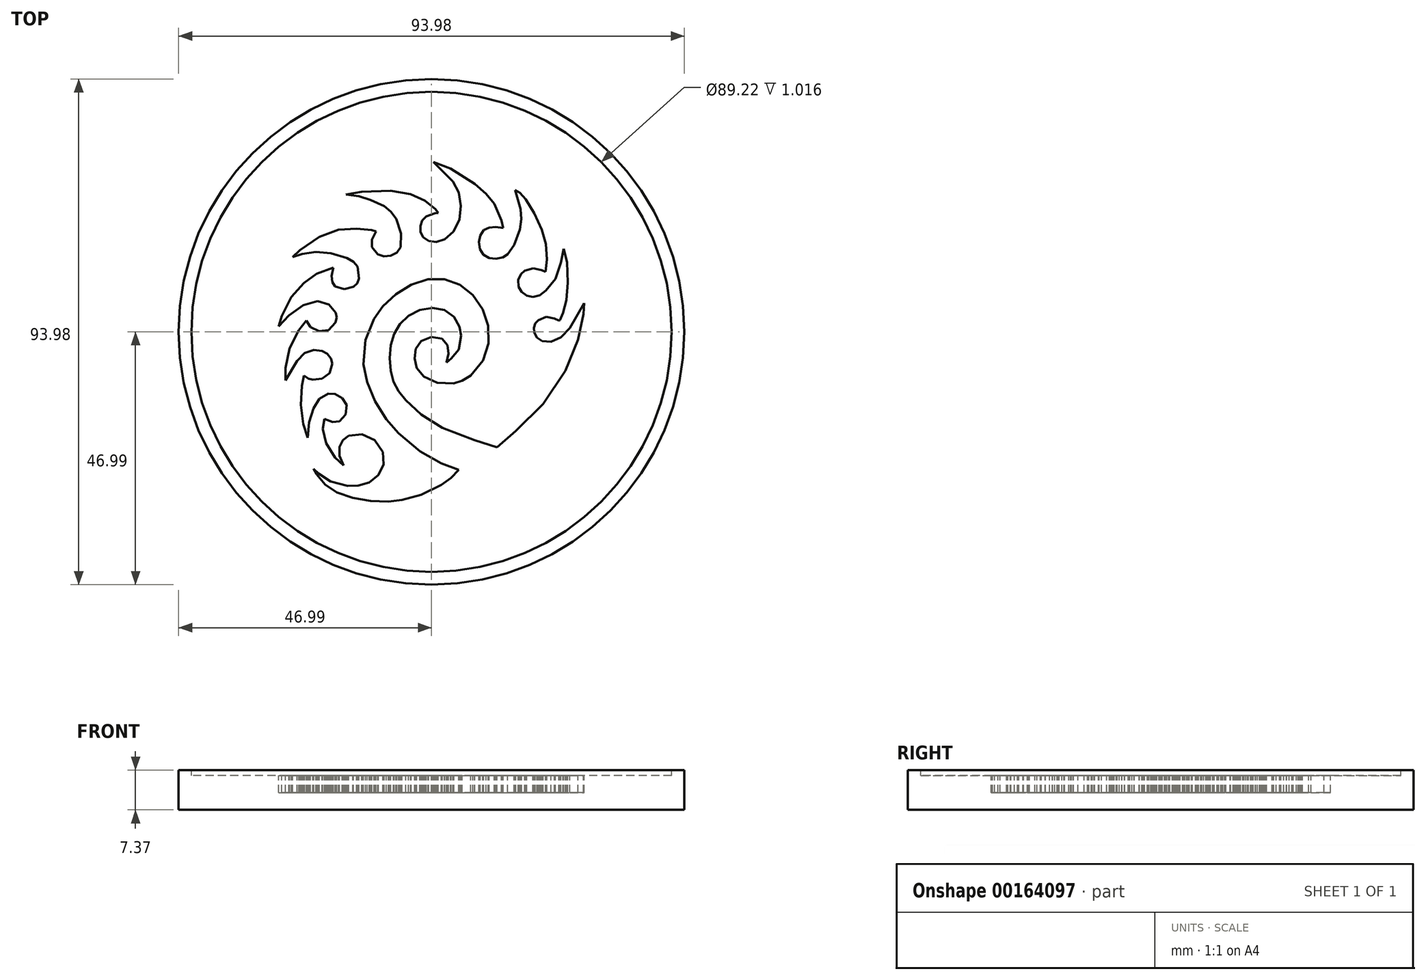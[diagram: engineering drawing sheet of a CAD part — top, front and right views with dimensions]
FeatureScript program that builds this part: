
annotation { "Feature Type Name" : "Feature", "Feature Type Description" : "" }
export const myFeature = defineFeature(function(context is Context, id is Id, definition is map)
    precondition{}
    {
        {
            var Q0;
            Q0=qCreatedBy(makeId("Front.planeOp"),FACE);
            var sketch = newSketch(context, id + "F0", { "sketchPlane" : qUnion([Q0])});
            skLineSegment(sketch, "E0", {"start": v(-47, 7.37) * mm, "end": v(-44.6, 7.37) * mm});
            skLineSegment(sketch, "E1", {"start": v(-44.6, 7.37) * mm, "end": v(-44.6, 6.35) * mm});
            skLineSegment(sketch, "E2", {"start": v(-44.6, 6.35) * mm, "end": v(0, 6.35) * mm});
            skLineSegment(sketch, "E3", {"start": v(0, 6.35) * mm, "end": v(0, 0) * mm});
            skLineSegment(sketch, "E4", {"start": v(0, 0) * mm, "end": v(-47, 0) * mm});
            skLineSegment(sketch, "E5", {"start": v(-47, 0) * mm, "end": v(-47, 7.37) * mm});
            skSolve(sketch);
        }
        {
            var Q0;
            Q0=makeQuery(id+"F0.imprint","IMPRINT",FACE,{"disambiguationData":[TD([[makeQuery(id+"F0.imprint","IMPRINT",EDGE,{"derivedFrom":sQuery(id+"F0.wireOp",EDGE,"E0")}),-1.0]])]});
            var Q1;
            Q1=sQuery(id+"F0.wireOp",EDGE,"E3");
            revolve(context, id + "F1", {"entities" : qUnion([Q0]), "axis" : qUnion([Q1]), "revolveType" : RevolveType.FULL});
        }
        {
            var Q0;
            Q0=makeQuery(id+"F1.opRevolve","SWEPT_FACE",FACE,{"disambiguationData":[OSD([sQuery(id+"F0.wireOp",EDGE,"E2")])]});
            var sketch = newSketch(context, id + "F2", { "sketchPlane" : qUnion([Q0])});
            skLineSegment(sketch, "E6", {"start": v(3.51, 30.35) * mm, "end": v(8.02, 27.48) * mm});
            skLineSegment(sketch, "E7", {"start": v(8.02, 27.48) * mm, "end": v(10.13, 25.64) * mm});
            skLineSegment(sketch, "E8", {"start": v(10.13, 25.64) * mm, "end": v(11.64, 23.83) * mm});
            skLineSegment(sketch, "E9", {"start": v(11.64, 23.83) * mm, "end": v(13.01, 20.73) * mm});
            skLineSegment(sketch, "E10", {"start": v(13.01, 20.73) * mm, "end": v(13.3, 19.34) * mm});
            skLineSegment(sketch, "E11", {"start": v(13.3, 19.34) * mm, "end": v(11.92, 19.48) * mm});
            skLineSegment(sketch, "E12", {"start": v(11.92, 19.48) * mm, "end": v(10.73, 19.38) * mm});
            skLineSegment(sketch, "E13", {"start": v(10.73, 19.38) * mm, "end": v(9.7, 18.9) * mm});
            skLineSegment(sketch, "E14", {"start": v(9.7, 18.9) * mm, "end": v(9.07, 17.93) * mm});
            skLineSegment(sketch, "E15", {"start": v(9.07, 17.93) * mm, "end": v(8.83, 16.67) * mm});
            skLineSegment(sketch, "E16", {"start": v(8.83, 16.67) * mm, "end": v(9.01, 15.38) * mm});
            skLineSegment(sketch, "E17", {"start": v(9.01, 15.38) * mm, "end": v(9.65, 14.33) * mm});
            skLineSegment(sketch, "E18", {"start": v(9.65, 14.33) * mm, "end": v(10.72, 13.72) * mm});
            skLineSegment(sketch, "E19", {"start": v(10.72, 13.72) * mm, "end": v(12, 13.57) * mm});
            skLineSegment(sketch, "E20", {"start": v(12, 13.57) * mm, "end": v(13.24, 13.81) * mm});
            skLineSegment(sketch, "E21", {"start": v(13.24, 13.81) * mm, "end": v(14.14, 14.4) * mm});
            skLineSegment(sketch, "E22", {"start": v(14.14, 14.4) * mm, "end": v(15.38, 16.13) * mm});
            skLineSegment(sketch, "E23", {"start": v(15.38, 16.13) * mm, "end": v(16.44, 19.06) * mm});
            skLineSegment(sketch, "E24", {"start": v(16.44, 19.06) * mm, "end": v(16.7, 20.97) * mm});
            skLineSegment(sketch, "E25", {"start": v(16.7, 20.97) * mm, "end": v(16.58, 22.8) * mm});
            skLineSegment(sketch, "E26", {"start": v(16.58, 22.8) * mm, "end": v(15.56, 26.32) * mm});
            skLineSegment(sketch, "E27", {"start": v(15.56, 26.32) * mm, "end": v(16.4, 25.85) * mm});
            skLineSegment(sketch, "E28", {"start": v(16.4, 25.85) * mm, "end": v(17.54, 24.62) * mm});
            skLineSegment(sketch, "E29", {"start": v(17.54, 24.62) * mm, "end": v(19.11, 22.05) * mm});
            skLineSegment(sketch, "E30", {"start": v(19.11, 22.05) * mm, "end": v(20.52, 18.99) * mm});
            skLineSegment(sketch, "E31", {"start": v(20.52, 18.99) * mm, "end": v(21.26, 16.32) * mm});
            skLineSegment(sketch, "E32", {"start": v(21.26, 16.32) * mm, "end": v(21.47, 13.44) * mm});
            skLineSegment(sketch, "E33", {"start": v(21.47, 13.44) * mm, "end": v(21.2, 11.14) * mm});
            skLineSegment(sketch, "E34", {"start": v(21.2, 11.14) * mm, "end": v(20.38, 11.51) * mm});
            skLineSegment(sketch, "E35", {"start": v(20.38, 11.51) * mm, "end": v(18.88, 11.82) * mm});
            skLineSegment(sketch, "E36", {"start": v(18.88, 11.82) * mm, "end": v(17.3, 11.38) * mm});
            skLineSegment(sketch, "E37", {"start": v(17.3, 11.38) * mm, "end": v(16.6, 10.73) * mm});
            skLineSegment(sketch, "E38", {"start": v(16.6, 10.73) * mm, "end": v(16.13, 9.64) * mm});
            skLineSegment(sketch, "E39", {"start": v(16.13, 9.64) * mm, "end": v(16.15, 8.39) * mm});
            skLineSegment(sketch, "E40", {"start": v(16.15, 8.39) * mm, "end": v(16.72, 7.4) * mm});
            skLineSegment(sketch, "E41", {"start": v(16.72, 7.4) * mm, "end": v(17.67, 6.75) * mm});
            skLineSegment(sketch, "E42", {"start": v(17.67, 6.75) * mm, "end": v(18.87, 6.5) * mm});
            skLineSegment(sketch, "E43", {"start": v(18.87, 6.5) * mm, "end": v(20.1, 6.82) * mm});
            skLineSegment(sketch, "E44", {"start": v(20.1, 6.82) * mm, "end": v(21.26, 7.67) * mm});
            skLineSegment(sketch, "E45", {"start": v(21.26, 7.67) * mm, "end": v(23.02, 9.87) * mm});
            skLineSegment(sketch, "E46", {"start": v(23.02, 9.87) * mm, "end": v(24.07, 12.88) * mm});
            skLineSegment(sketch, "E47", {"start": v(24.07, 12.88) * mm, "end": v(24.53, 15.44) * mm});
            skLineSegment(sketch, "E48", {"start": v(24.53, 15.44) * mm, "end": v(25.18, 12.95) * mm});
            skLineSegment(sketch, "E49", {"start": v(25.18, 12.95) * mm, "end": v(25.34, 9.11) * mm});
            skLineSegment(sketch, "E50", {"start": v(25.34, 9.11) * mm, "end": v(25.05, 5.9) * mm});
            skLineSegment(sketch, "E51", {"start": v(25.05, 5.9) * mm, "end": v(24.41, 3.51) * mm});
            skLineSegment(sketch, "E52", {"start": v(24.41, 3.51) * mm, "end": v(23.83, 2.2) * mm});
            skLineSegment(sketch, "E53", {"start": v(23.83, 2.2) * mm, "end": v(23.67, 2.11) * mm});
            skLineSegment(sketch, "E54", {"start": v(23.67, 2.11) * mm, "end": v(22.83, 2.47) * mm});
            skLineSegment(sketch, "E55", {"start": v(22.83, 2.47) * mm, "end": v(21.3, 2.77) * mm});
            skLineSegment(sketch, "E56", {"start": v(21.3, 2.77) * mm, "end": v(19.84, 2.17) * mm});
            skLineSegment(sketch, "E57", {"start": v(19.84, 2.17) * mm, "end": v(19.27, 1.56) * mm});
            skLineSegment(sketch, "E58", {"start": v(19.27, 1.56) * mm, "end": v(19.02, 0.78) * mm});
            skLineSegment(sketch, "E59", {"start": v(19.02, 0.78) * mm, "end": v(19.11, -0.16) * mm});
            skLineSegment(sketch, "E60", {"start": v(19.11, -0.16) * mm, "end": v(19.59, -1.07) * mm});
            skLineSegment(sketch, "E61", {"start": v(19.59, -1.07) * mm, "end": v(20.57, -1.73) * mm});
            skLineSegment(sketch, "E62", {"start": v(20.57, -1.73) * mm, "end": v(22.18, -1.86) * mm});
            skLineSegment(sketch, "E63", {"start": v(22.18, -1.86) * mm, "end": v(24.06, -1.05) * mm});
            skLineSegment(sketch, "E64", {"start": v(24.06, -1.05) * mm, "end": v(25.71, 0.7) * mm});
            skLineSegment(sketch, "E65", {"start": v(25.71, 0.7) * mm, "end": v(28.38, 5.32) * mm});
            skLineSegment(sketch, "E66", {"start": v(28.38, 5.32) * mm, "end": v(28.23, 3.3) * mm});
            skLineSegment(sketch, "E67", {"start": v(28.23, 3.3) * mm, "end": v(27.24, -1.5) * mm});
            skLineSegment(sketch, "E68", {"start": v(27.24, -1.5) * mm, "end": v(24.85, -7.22) * mm});
            skLineSegment(sketch, "E69", {"start": v(24.85, -7.22) * mm, "end": v(20.72, -13.37) * mm});
            skLineSegment(sketch, "E70", {"start": v(20.72, -13.37) * mm, "end": v(15.7, -18.4) * mm});
            skLineSegment(sketch, "E71", {"start": v(15.7, -18.4) * mm, "end": v(12.17, -21.48) * mm});
            skLineSegment(sketch, "E72", {"start": v(12.17, -21.48) * mm, "end": v(8, -20.13) * mm});
            skLineSegment(sketch, "E73", {"start": v(8, -20.13) * mm, "end": v(2.04, -17.87) * mm});
            skLineSegment(sketch, "E74", {"start": v(2.04, -17.87) * mm, "end": v(-1.91, -15.38) * mm});
            skLineSegment(sketch, "E75", {"start": v(-1.91, -15.38) * mm, "end": v(-4.77, -12.71) * mm});
            skLineSegment(sketch, "E76", {"start": v(-4.77, -12.71) * mm, "end": v(-6.12, -11.02) * mm});
            skLineSegment(sketch, "E77", {"start": v(-6.12, -11.02) * mm, "end": v(-7.05, -9.25) * mm});
            skLineSegment(sketch, "E78", {"start": v(-7.05, -9.25) * mm, "end": v(-7.6, -7.25) * mm});
            skLineSegment(sketch, "E79", {"start": v(-7.6, -7.25) * mm, "end": v(-7.8, -4.9) * mm});
            skLineSegment(sketch, "E80", {"start": v(-7.8, -4.9) * mm, "end": v(-7.6, -2.48) * mm});
            skLineSegment(sketch, "E81", {"start": v(-7.6, -2.48) * mm, "end": v(-6.96, -0.37) * mm});
            skLineSegment(sketch, "E82", {"start": v(-6.96, -0.37) * mm, "end": v(-5.85, 1.44) * mm});
            skLineSegment(sketch, "E83", {"start": v(-5.85, 1.44) * mm, "end": v(-4.26, 2.97) * mm});
            skLineSegment(sketch, "E84", {"start": v(-4.26, 2.97) * mm, "end": v(-2.17, 4.06) * mm});
            skLineSegment(sketch, "E85", {"start": v(-2.17, 4.06) * mm, "end": v(0.18, 4.47) * mm});
            skLineSegment(sketch, "E86", {"start": v(0.18, 4.47) * mm, "end": v(2.43, 4.07) * mm});
            skLineSegment(sketch, "E87", {"start": v(2.43, 4.07) * mm, "end": v(4.18, 2.76) * mm});
            skLineSegment(sketch, "E88", {"start": v(4.18, 2.76) * mm, "end": v(5.18, 0.98) * mm});
            skLineSegment(sketch, "E89", {"start": v(5.18, 0.98) * mm, "end": v(5.52, -0.7) * mm});
            skLineSegment(sketch, "E90", {"start": v(5.52, -0.7) * mm, "end": v(5.04, -3.27) * mm});
            skLineSegment(sketch, "E91", {"start": v(5.04, -3.27) * mm, "end": v(3.7, -4.95) * mm});
            skLineSegment(sketch, "E92", {"start": v(3.7, -4.95) * mm, "end": v(2.76, -5.74) * mm});
            skLineSegment(sketch, "E93", {"start": v(2.76, -5.74) * mm, "end": v(3.18, -4.05) * mm});
            skLineSegment(sketch, "E94", {"start": v(3.18, -4.05) * mm, "end": v(2.95, -2.45) * mm});
            skLineSegment(sketch, "E95", {"start": v(2.95, -2.45) * mm, "end": v(1.94, -1.3) * mm});
            skLineSegment(sketch, "E96", {"start": v(1.94, -1.3) * mm, "end": v(0, -0.98) * mm});
            skLineSegment(sketch, "E97", {"start": v(0, -0.98) * mm, "end": v(-1.94, -1.7) * mm});
            skLineSegment(sketch, "E98", {"start": v(-1.94, -1.7) * mm, "end": v(-2.93, -3.17) * mm});
            skLineSegment(sketch, "E99", {"start": v(-2.93, -3.17) * mm, "end": v(-3.15, -4.98) * mm});
            skLineSegment(sketch, "E100", {"start": v(-3.15, -4.98) * mm, "end": v(-2.78, -6.74) * mm});
            skLineSegment(sketch, "E101", {"start": v(-2.78, -6.74) * mm, "end": v(-1.43, -8.31) * mm});
            skLineSegment(sketch, "E102", {"start": v(-1.43, -8.31) * mm, "end": v(1.04, -9.45) * mm});
            skLineSegment(sketch, "E103", {"start": v(1.04, -9.45) * mm, "end": v(4.11, -9.57) * mm});
            skLineSegment(sketch, "E104", {"start": v(4.11, -9.57) * mm, "end": v(5.7, -9.07) * mm});
            skLineSegment(sketch, "E105", {"start": v(5.7, -9.07) * mm, "end": v(7.26, -8.1) * mm});
            skLineSegment(sketch, "E106", {"start": v(7.26, -8.1) * mm, "end": v(9.58, -5.33) * mm});
            skLineSegment(sketch, "E107", {"start": v(9.58, -5.33) * mm, "end": v(10.62, -2.16) * mm});
            skLineSegment(sketch, "E108", {"start": v(10.62, -2.16) * mm, "end": v(10.53, 1.12) * mm});
            skLineSegment(sketch, "E109", {"start": v(10.53, 1.12) * mm, "end": v(9.47, 4.22) * mm});
            skLineSegment(sketch, "E110", {"start": v(9.47, 4.22) * mm, "end": v(7.64, 6.84) * mm});
            skLineSegment(sketch, "E111", {"start": v(7.64, 6.84) * mm, "end": v(5.23, 8.75) * mm});
            skLineSegment(sketch, "E112", {"start": v(5.23, 8.75) * mm, "end": v(2.42, 9.79) * mm});
            skLineSegment(sketch, "E113", {"start": v(2.42, 9.79) * mm, "end": v(-0.63, 9.8) * mm});
            skLineSegment(sketch, "E114", {"start": v(-0.63, 9.8) * mm, "end": v(-3.74, 8.76) * mm});
            skLineSegment(sketch, "E115", {"start": v(-3.74, 8.76) * mm, "end": v(-6.65, 7) * mm});
            skLineSegment(sketch, "E116", {"start": v(-6.65, 7) * mm, "end": v(-9.07, 4.78) * mm});
            skLineSegment(sketch, "E117", {"start": v(-9.07, 4.78) * mm, "end": v(-10.69, 2.41) * mm});
            skLineSegment(sketch, "E118", {"start": v(-10.69, 2.41) * mm, "end": v(-12.3, -1.5) * mm});
            skLineSegment(sketch, "E119", {"start": v(-12.3, -1.5) * mm, "end": v(-12.63, -6.04) * mm});
            skLineSegment(sketch, "E120", {"start": v(-12.63, -6.04) * mm, "end": v(-11.97, -9.33) * mm});
            skLineSegment(sketch, "E121", {"start": v(-11.97, -9.33) * mm, "end": v(-10.47, -12.92) * mm});
            skLineSegment(sketch, "E122", {"start": v(-10.47, -12.92) * mm, "end": v(-8.42, -16.27) * mm});
            skLineSegment(sketch, "E123", {"start": v(-8.42, -16.27) * mm, "end": v(-6.1, -18.87) * mm});
            skLineSegment(sketch, "E124", {"start": v(-6.1, -18.87) * mm, "end": v(-2.1, -22.2) * mm});
            skLineSegment(sketch, "E125", {"start": v(-2.1, -22.2) * mm, "end": v(1.82, -24.44) * mm});
            skLineSegment(sketch, "E126", {"start": v(1.82, -24.44) * mm, "end": v(5.09, -25.63) * mm});
            skLineSegment(sketch, "E127", {"start": v(5.09, -25.63) * mm, "end": v(3.59, -27.18) * mm});
            skLineSegment(sketch, "E128", {"start": v(3.59, -27.18) * mm, "end": v(1.85, -28.46) * mm});
            skLineSegment(sketch, "E129", {"start": v(1.85, -28.46) * mm, "end": v(-1.93, -30.28) * mm});
            skLineSegment(sketch, "E130", {"start": v(-1.93, -30.28) * mm, "end": v(-5.47, -31.26) * mm});
            skLineSegment(sketch, "E131", {"start": v(-5.47, -31.26) * mm, "end": v(-8, -31.56) * mm});
            skLineSegment(sketch, "E132", {"start": v(-8, -31.56) * mm, "end": v(-11.35, -31.46) * mm});
            skLineSegment(sketch, "E133", {"start": v(-11.35, -31.46) * mm, "end": v(-14.65, -30.88) * mm});
            skLineSegment(sketch, "E134", {"start": v(-14.65, -30.88) * mm, "end": v(-17.6, -29.85) * mm});
            skLineSegment(sketch, "E135", {"start": v(-17.6, -29.85) * mm, "end": v(-19.79, -28.4) * mm});
            skLineSegment(sketch, "E136", {"start": v(-19.79, -28.4) * mm, "end": v(-21.35, -26.49) * mm});
            skLineSegment(sketch, "E137", {"start": v(-21.35, -26.49) * mm, "end": v(-21.93, -25.47) * mm});
            skLineSegment(sketch, "E138", {"start": v(-21.93, -25.47) * mm, "end": v(-20.98, -26.38) * mm});
            skLineSegment(sketch, "E139", {"start": v(-20.98, -26.38) * mm, "end": v(-18.75, -27.82) * mm});
            skLineSegment(sketch, "E140", {"start": v(-18.75, -27.82) * mm, "end": v(-15.57, -28.65) * mm});
            skLineSegment(sketch, "E141", {"start": v(-15.57, -28.65) * mm, "end": v(-13.64, -28.6) * mm});
            skLineSegment(sketch, "E142", {"start": v(-13.64, -28.6) * mm, "end": v(-11.59, -27.99) * mm});
            skLineSegment(sketch, "E143", {"start": v(-11.59, -27.99) * mm, "end": v(-9.83, -26.61) * mm});
            skLineSegment(sketch, "E144", {"start": v(-9.83, -26.61) * mm, "end": v(-8.9, -24.63) * mm});
            skLineSegment(sketch, "E145", {"start": v(-8.9, -24.63) * mm, "end": v(-9.07, -22.36) * mm});
            skLineSegment(sketch, "E146", {"start": v(-9.07, -22.36) * mm, "end": v(-10.56, -20.12) * mm});
            skLineSegment(sketch, "E147", {"start": v(-10.56, -20.12) * mm, "end": v(-12.9, -19.03) * mm});
            skLineSegment(sketch, "E148", {"start": v(-12.9, -19.03) * mm, "end": v(-15.38, -19.3) * mm});
            skLineSegment(sketch, "E149", {"start": v(-15.38, -19.3) * mm, "end": v(-16.47, -20.12) * mm});
            skLineSegment(sketch, "E150", {"start": v(-16.47, -20.12) * mm, "end": v(-17.1, -21.41) * mm});
            skLineSegment(sketch, "E151", {"start": v(-17.1, -21.41) * mm, "end": v(-17.1, -23.03) * mm});
            skLineSegment(sketch, "E152", {"start": v(-17.1, -23.03) * mm, "end": v(-16.34, -24.82) * mm});
            skLineSegment(sketch, "E153", {"start": v(-16.34, -24.82) * mm, "end": v(-18.09, -23.24) * mm});
            skLineSegment(sketch, "E154", {"start": v(-17.94, -23.37) * mm, "end": v(-19.55, -20.68) * mm});
            skLineSegment(sketch, "E155", {"start": v(-19.55, -20.68) * mm, "end": v(-20.2, -18.01) * mm});
            skLineSegment(sketch, "E156", {"start": v(-20.2, -18.01) * mm, "end": v(-19.9, -16.2) * mm});
            skLineSegment(sketch, "E157", {"start": v(-19.9, -16.2) * mm, "end": v(-18.39, -16.79) * mm});
            skLineSegment(sketch, "E158", {"start": v(-18.39, -16.79) * mm, "end": v(-17.09, -16.63) * mm});
            skLineSegment(sketch, "E159", {"start": v(-17.09, -16.63) * mm, "end": v(-15.95, -15.4) * mm});
            skLineSegment(sketch, "E160", {"start": v(-15.95, -15.4) * mm, "end": v(-15.74, -13.6) * mm});
            skLineSegment(sketch, "E161", {"start": v(-15.74, -13.6) * mm, "end": v(-16.58, -12.3) * mm});
            skLineSegment(sketch, "E162", {"start": v(-16.58, -12.3) * mm, "end": v(-17.92, -11.56) * mm});
            skLineSegment(sketch, "E163", {"start": v(-17.92, -11.56) * mm, "end": v(-19.21, -11.48) * mm});
            skLineSegment(sketch, "E164", {"start": v(-19.21, -11.48) * mm, "end": v(-20.82, -12.44) * mm});
            skLineSegment(sketch, "E165", {"start": v(-20.82, -12.44) * mm, "end": v(-21.92, -14.25) * mm});
            skLineSegment(sketch, "E166", {"start": v(-21.92, -14.25) * mm, "end": v(-22.75, -16.82) * mm});
            skLineSegment(sketch, "E167", {"start": v(-22.75, -16.82) * mm, "end": v(-22.98, -19.69) * mm});
            skLineSegment(sketch, "E168", {"start": v(-22.98, -19.69) * mm, "end": v(-23.83, -17.13) * mm});
            skLineSegment(sketch, "E169", {"start": v(-23.83, -17.13) * mm, "end": v(-24.26, -13.56) * mm});
            skLineSegment(sketch, "E170", {"start": v(-24.26, -13.56) * mm, "end": v(-24.1, -10.04) * mm});
            skLineSegment(sketch, "E171", {"start": v(-24.1, -10.04) * mm, "end": v(-23.7, -8.14) * mm});
            skLineSegment(sketch, "E172", {"start": v(-23.7, -8.14) * mm, "end": v(-22.88, -8.7) * mm});
            skLineSegment(sketch, "E173", {"start": v(-22.88, -8.7) * mm, "end": v(-22.02, -8.9) * mm});
            skLineSegment(sketch, "E174", {"start": v(-22.02, -8.9) * mm, "end": v(-20.32, -8.68) * mm});
            skLineSegment(sketch, "E175", {"start": v(-20.32, -8.68) * mm, "end": v(-18.92, -7.7) * mm});
            skLineSegment(sketch, "E176", {"start": v(-18.92, -7.7) * mm, "end": v(-18.43, -5.9) * mm});
            skLineSegment(sketch, "E177", {"start": v(-18.43, -5.9) * mm, "end": v(-18.66, -4.93) * mm});
            skLineSegment(sketch, "E178", {"start": v(-18.66, -4.93) * mm, "end": v(-19.38, -4.05) * mm});
            skLineSegment(sketch, "E179", {"start": v(-19.38, -4.05) * mm, "end": v(-20.32, -3.55) * mm});
            skLineSegment(sketch, "E180", {"start": v(-20.32, -3.55) * mm, "end": v(-21.88, -3.38) * mm});
            skLineSegment(sketch, "E181", {"start": v(-21.88, -3.38) * mm, "end": v(-23.6, -3.95) * mm});
            skLineSegment(sketch, "E182", {"start": v(-23.6, -3.95) * mm, "end": v(-24.97, -5.39) * mm});
            skLineSegment(sketch, "E183", {"start": v(-24.97, -5.39) * mm, "end": v(-27.13, -9.02) * mm});
            skLineSegment(sketch, "E184", {"start": v(-27.13, -9.02) * mm, "end": v(-27.14, -6.7) * mm});
            skLineSegment(sketch, "E185", {"start": v(-27.14, -6.7) * mm, "end": v(-26.38, -3.04) * mm});
            skLineSegment(sketch, "E186", {"start": v(-26.38, -3.04) * mm, "end": v(-24.69, 0.3) * mm});
            skLineSegment(sketch, "E187", {"start": v(-24.69, 0.3) * mm, "end": v(-23.25, 2.11) * mm});
            skLineSegment(sketch, "E188", {"start": v(-23.25, 2.11) * mm, "end": v(-22.47, 0.92) * mm});
            skLineSegment(sketch, "E189", {"start": v(-22.47, 0.92) * mm, "end": v(-20.93, 0.11) * mm});
            skLineSegment(sketch, "E190", {"start": v(-20.93, 0.11) * mm, "end": v(-19.15, 0.3) * mm});
            skLineSegment(sketch, "E191", {"start": v(-19.15, 0.3) * mm, "end": v(-17.86, 1.7) * mm});
            skLineSegment(sketch, "E192", {"start": v(-17.86, 1.7) * mm, "end": v(-17.6, 2.65) * mm});
            skLineSegment(sketch, "E193", {"start": v(-17.6, 2.65) * mm, "end": v(-17.78, 3.58) * mm});
            skLineSegment(sketch, "E194", {"start": v(-17.78, 3.58) * mm, "end": v(-19.07, 5.1) * mm});
            skLineSegment(sketch, "E195", {"start": v(-19.07, 5.1) * mm, "end": v(-21.14, 5.7) * mm});
            skLineSegment(sketch, "E196", {"start": v(-21.14, 5.7) * mm, "end": v(-23.84, 4.95) * mm});
            skLineSegment(sketch, "E197", {"start": v(-23.84, 4.95) * mm, "end": v(-26.48, 3.02) * mm});
            skLineSegment(sketch, "E198", {"start": v(-26.48, 3.02) * mm, "end": v(-28.38, 1) * mm});
            skLineSegment(sketch, "E199", {"start": v(-28.38, 1) * mm, "end": v(-27.82, 2.94) * mm});
            skLineSegment(sketch, "E200", {"start": v(-27.82, 2.94) * mm, "end": v(-26.06, 6.45) * mm});
            skLineSegment(sketch, "E201", {"start": v(-26.06, 6.45) * mm, "end": v(-23.72, 9.1) * mm});
            skLineSegment(sketch, "E202", {"start": v(-23.72, 9.1) * mm, "end": v(-21.35, 10.78) * mm});
            skLineSegment(sketch, "E203", {"start": v(-21.35, 10.78) * mm, "end": v(-18.28, 11.93) * mm});
            skLineSegment(sketch, "E204", {"start": v(-18.28, 11.93) * mm, "end": v(-18.53, 10.44) * mm});
            skLineSegment(sketch, "E205", {"start": v(-18.53, 10.44) * mm, "end": v(-18.46, 9.27) * mm});
            skLineSegment(sketch, "E206", {"start": v(-18.46, 9.27) * mm, "end": v(-17.9, 8.45) * mm});
            skLineSegment(sketch, "E207", {"start": v(-17.9, 8.45) * mm, "end": v(-16.21, 7.97) * mm});
            skLineSegment(sketch, "E208", {"start": v(-16.21, 7.97) * mm, "end": v(-14.53, 8.4) * mm});
            skLineSegment(sketch, "E209", {"start": v(-14.53, 8.4) * mm, "end": v(-13.82, 9) * mm});
            skLineSegment(sketch, "E210", {"start": v(-13.82, 9) * mm, "end": v(-13.45, 9.94) * mm});
            skLineSegment(sketch, "E211", {"start": v(-13.45, 9.94) * mm, "end": v(-13.74, 12.1) * mm});
            skLineSegment(sketch, "E212", {"start": v(-13.74, 12.1) * mm, "end": v(-14.48, 13) * mm});
            skLineSegment(sketch, "E213", {"start": v(-14.48, 13) * mm, "end": v(-15.68, 13.7) * mm});
            skLineSegment(sketch, "E214", {"start": v(-15.68, 13.7) * mm, "end": v(-18.68, 14.59) * mm});
            skLineSegment(sketch, "E215", {"start": v(-18.68, 14.59) * mm, "end": v(-21.46, 14.83) * mm});
            skLineSegment(sketch, "E216", {"start": v(-21.46, 14.83) * mm, "end": v(-24.02, 14.48) * mm});
            skLineSegment(sketch, "E217", {"start": v(-24.02, 14.48) * mm, "end": v(-25.82, 13.88) * mm});
            skLineSegment(sketch, "E218", {"start": v(-25.82, 13.88) * mm, "end": v(-24.44, 15.2) * mm});
            skLineSegment(sketch, "E219", {"start": v(-24.44, 15.2) * mm, "end": v(-20.87, 17.62) * mm});
            skLineSegment(sketch, "E220", {"start": v(-20.87, 17.62) * mm, "end": v(-17.28, 18.96) * mm});
            skLineSegment(sketch, "E221", {"start": v(-17.28, 18.96) * mm, "end": v(-13.94, 19.2) * mm});
            skLineSegment(sketch, "E222", {"start": v(-13.94, 19.2) * mm, "end": v(-11.13, 18.93) * mm});
            skLineSegment(sketch, "E223", {"start": v(-11.13, 18.93) * mm, "end": v(-10.31, 18.66) * mm});
            skLineSegment(sketch, "E224", {"start": v(-10.31, 18.66) * mm, "end": v(-11.07, 17.15) * mm});
            skLineSegment(sketch, "E225", {"start": v(-11.07, 17.15) * mm, "end": v(-11.1, 15.76) * mm});
            skLineSegment(sketch, "E226", {"start": v(-11.1, 15.76) * mm, "end": v(-9.97, 14.38) * mm});
            skLineSegment(sketch, "E227", {"start": v(-9.97, 14.38) * mm, "end": v(-8.85, 14) * mm});
            skLineSegment(sketch, "E228", {"start": v(-8.85, 14) * mm, "end": v(-7.56, 14.14) * mm});
            skLineSegment(sketch, "E229", {"start": v(-7.56, 14.14) * mm, "end": v(-6.41, 14.74) * mm});
            skLineSegment(sketch, "E230", {"start": v(-6.41, 14.74) * mm, "end": v(-5.72, 15.75) * mm});
            skLineSegment(sketch, "E231", {"start": v(-5.72, 15.75) * mm, "end": v(-5.66, 18.31) * mm});
            skLineSegment(sketch, "E232", {"start": v(-5.66, 18.31) * mm, "end": v(-6.59, 21.01) * mm});
            skLineSegment(sketch, "E233", {"start": v(-6.59, 21.01) * mm, "end": v(-7.56, 22.35) * mm});
            skLineSegment(sketch, "E234", {"start": v(-7.56, 22.35) * mm, "end": v(-8.77, 23.36) * mm});
            skLineSegment(sketch, "E235", {"start": v(-8.77, 23.36) * mm, "end": v(-11.31, 24.54) * mm});
            skLineSegment(sketch, "E236", {"start": v(-11.31, 24.54) * mm, "end": v(-13.48, 25.19) * mm});
            skLineSegment(sketch, "E237", {"start": v(-13.48, 25.19) * mm, "end": v(-15.88, 25.53) * mm});
            skLineSegment(sketch, "E238", {"start": v(-15.88, 25.53) * mm, "end": v(-13, 26) * mm});
            skLineSegment(sketch, "E239", {"start": v(-13, 26) * mm, "end": v(-7.6, 26.2) * mm});
            skLineSegment(sketch, "E240", {"start": v(-7.6, 26.2) * mm, "end": v(-3.86, 25.58) * mm});
            skLineSegment(sketch, "E241", {"start": v(-3.86, 25.58) * mm, "end": v(-1.24, 24.38) * mm});
            skLineSegment(sketch, "E242", {"start": v(-1.24, 24.38) * mm, "end": v(0.71, 22.8) * mm});
            skLineSegment(sketch, "E243", {"start": v(0.71, 22.8) * mm, "end": v(1.28, 22.08) * mm});
            skLineSegment(sketch, "E244", {"start": v(1.28, 22.08) * mm, "end": v(0.59, 22.04) * mm});
            skLineSegment(sketch, "E245", {"start": v(0.59, 22.04) * mm, "end": v(-1, 21.45) * mm});
            skLineSegment(sketch, "E246", {"start": v(-1, 21.45) * mm, "end": v(-1.71, 20.7) * mm});
            skLineSegment(sketch, "E247", {"start": v(-1.71, 20.7) * mm, "end": v(-2.07, 19.66) * mm});
            skLineSegment(sketch, "E248", {"start": v(-2.07, 19.66) * mm, "end": v(-2.03, 18.55) * mm});
            skLineSegment(sketch, "E249", {"start": v(-2.03, 18.55) * mm, "end": v(-1.55, 17.56) * mm});
            skLineSegment(sketch, "E250", {"start": v(-1.55, 17.56) * mm, "end": v(-0.56, 16.88) * mm});
            skLineSegment(sketch, "E251", {"start": v(-0.56, 16.88) * mm, "end": v(0.86, 16.7) * mm});
            skLineSegment(sketch, "E252", {"start": v(0.86, 16.7) * mm, "end": v(2.48, 17.2) * mm});
            skLineSegment(sketch, "E253", {"start": v(2.48, 17.2) * mm, "end": v(4.08, 18.58) * mm});
            skLineSegment(sketch, "E254", {"start": v(4.08, 18.58) * mm, "end": v(5.17, 20.8) * mm});
            skLineSegment(sketch, "E255", {"start": v(5.17, 20.8) * mm, "end": v(5.47, 23.4) * mm});
            skLineSegment(sketch, "E256", {"start": v(5.47, 23.4) * mm, "end": v(5.04, 25.92) * mm});
            skLineSegment(sketch, "E257", {"start": v(5.04, 25.92) * mm, "end": v(3.96, 27.92) * mm});
            skLineSegment(sketch, "E258", {"start": v(3.96, 27.92) * mm, "end": v(0.34, 31.56) * mm});
            skLineSegment(sketch, "E259", {"start": v(0.34, 31.56) * mm, "end": v(3.51, 30.35) * mm});
            skSolve(sketch);
        }
        {
            var Q0;
            Q0 = qSketchRegion(id + "F2", true);
            extrude(context, id + "F3", {"entities" : qUnion([Q0]), "operationType" : NewBodyOperationType.REMOVE, "oppositeDirection" : true, "depth" : 3.17 * mm});
        }
    });
